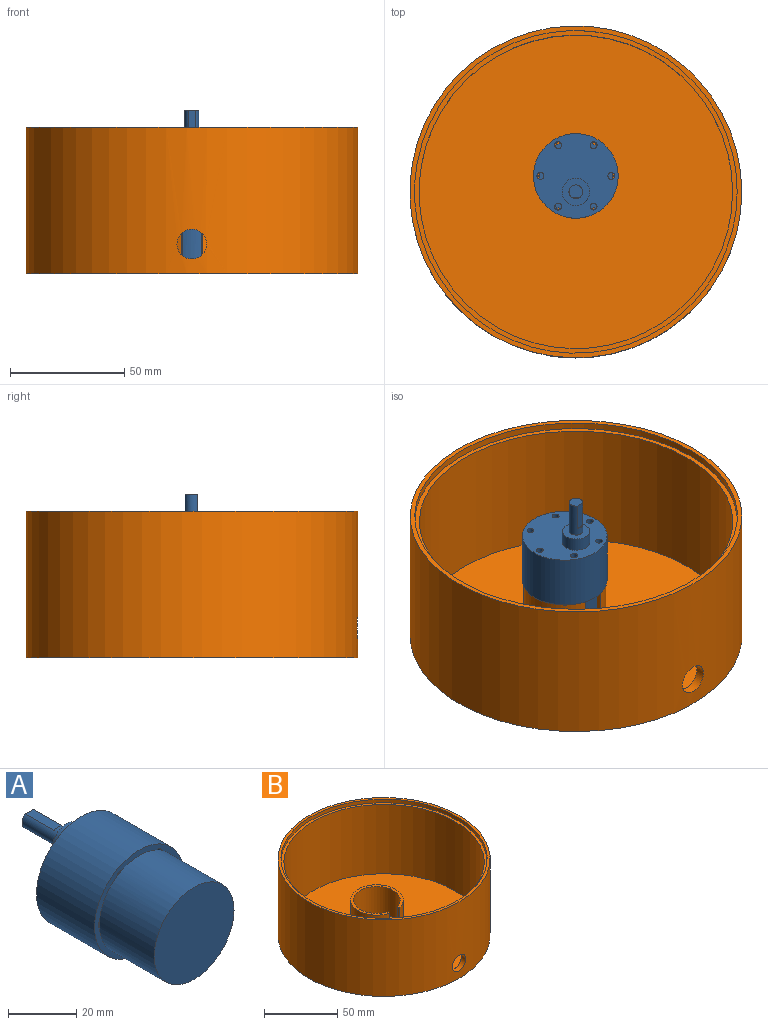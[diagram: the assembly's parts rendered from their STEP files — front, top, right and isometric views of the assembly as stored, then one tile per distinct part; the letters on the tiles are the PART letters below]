
ASSEMBLY  parts=2 mates=1
PART A: 23 faces, bbox 37x68.2x37 mm
  f0: plane 6x5.5mm, normal (0,1,0), area 27.1mm2, adj f12,f13
  f1: cylinder r=1.5mm len=24mm, axis (0,1,0), area 226.2mm2, adj f8,f9,f22
  f2: cylinder r=1.5mm len=24mm, axis (0,1,0), area 226.2mm2, adj f8,f9,f19
  f3: cylinder r=1.5mm len=24mm, axis (0,1,0), area 226.2mm2, adj f8,f9,f18
  f4: cylinder r=1.5mm len=24mm, axis (0,1,0), area 226.2mm2, adj f8,f9,f17
  f5: cylinder r=1.5mm len=24mm, axis (0,1,0), area 226.2mm2, adj f8,f9,f16
  f6: cylinder r=1.5mm len=24mm, axis (0,1,0), area 226.2mm2, adj f8,f9,f15
  f7: cylinder r=18.5mm len=37mm, axis (0,1,0), area 2789.7mm2, adj f8,f9
  f8: plane 37x37mm, normal (0,-1,0), area 215.1mm2, adj f1,f2,f3,f4,f5,f6,f7,f20
  f9: plane 37x37mm, normal (0,1,0), area 919.7mm2, adj f1,f2,f3,f4,f5,f6,f7,f10
  f10: cylinder r=6mm len=12mm, axis (0,-1,0), area 226.2mm2, adj f9,f11
  f11: plane 12x12mm, normal (0,1,0), area 84.8mm2, adj f10,f12
  f12: cylinder r=3mm len=15.5mm, axis (0,-1,0), area 250mm2, adj f0,f11,f13,f14
  f13: plane 12x3.32mm, normal (0,0,1), area 39.8mm2, adj f0,f12,f14
  f14: plane 3.32x0.5mm, normal (0,1,0), area 1.1mm2, adj f12,f13
  f15: plane 3x2.91mm, normal (0,1,0), area 6.3mm2, adj f6,f20
  f16: plane 3x2.91mm, normal (0,1,0), area 6.3mm2, adj f5,f20
  f17: plane 3x2.5mm, normal (0,1,0), area 6.3mm2, adj f4,f20
  f18: plane 3x2.91mm, normal (0,1,0), area 6.3mm2, adj f3,f20
  f19: plane 3x2.91mm, normal (0,1,0), area 6.3mm2, adj f2,f20
  f20: cylinder r=16.5mm len=33mm, axis (0,1,0), area 2353.4mm2, adj f8,f15,f16,f17,f18,f19,f21,f22
  f21: plane 33x33mm, normal (0,-1,0), area 855.3mm2, adj f20
  f22: plane 3x2.5mm, normal (0,1,0), area 6.3mm2, adj f1,f20
PART B: 13 faces, bbox 145x145x64 mm
  f0: plane 137x137mm, normal (0,0,1), area 14545.3mm2, adj f5,f7,f8,f9,f10
  f1: cylinder r=70.5mm len=141mm, axis (0,0,-1), area 1328.9mm2, adj f3,f6
  f2: cylinder r=72.5mm len=145mm, axis (0,0,-1), area 29020.9mm2, adj f3,f4,f12
  f3: plane 145x145mm, normal (0,0,1), area 898.5mm2, adj f1,f2
  f4: plane 145x145mm, normal (0,0,-1), area 16513mm2, adj f2
  f5: cylinder r=68.5mm len=137mm, axis (0,0,-1), area 24830mm2, adj f0,f6,f12
  f6: plane 141x141mm, normal (0,0,1), area 873.4mm2, adj f1,f5
  f7: cylinder r=18mm len=36mm, axis (0,0,-1), area 2384.5mm2, adj f0,f8,f10,f11
  f8: plane 23x1.93mm, normal (0.97,-0.26,0), area 46mm2, adj f0,f7,f9,f11
  f9: cylinder r=16mm len=32mm, axis (0,0,-1), area 2119.5mm2, adj f0,f8,f10,f11
  f10: plane 23x1.93mm, normal (-0.97,-0.26,0), area 46mm2, adj f0,f7,f9,f11
  f11: plane 36x35.39mm, normal (0,0,1), area 195.8mm2, adj f7,f8,f9,f10
  f12: cylinder r=6.5mm len=13mm, axis (0,-1,0), area 163.7mm2, adj f2,f5
PLACE A rot(axis=(1,0,0),90deg) t=(0,7,50)mm
PLACE B at identity fixed
MATE revolute B.f7 <-> A.f7  axis (0,0,1) through (0,7,26)mm
